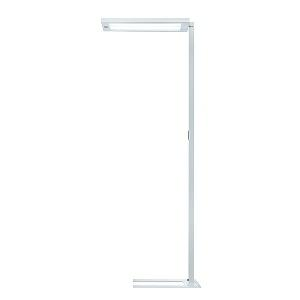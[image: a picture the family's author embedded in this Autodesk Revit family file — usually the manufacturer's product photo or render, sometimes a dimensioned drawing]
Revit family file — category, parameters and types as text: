
# Revit family: lavigo_-_dps_14000_840_r_g2_00725995_d7d4
name_source: partatom
category: Lighting Fixtures
units: mm (PartAtom-declared; Revit-internal decimal feet)

## family parameters
Cut with Voids When Loaded = No
Host = Face
Light Source = No
Part Type = Normal
Room Calculation Point = No
Round Connector Dimension = Use Diameter
Shared = No

## types (1)
- LAVIGO - DPS 14000/840/R/G2 (1 x LED, 14050 lm, 4000K)
    Apparent Load = 93 VA
    Approval mark = CE
    CIE Flux Codes = 60 87 97 12 100
    Color Rendering = 80-89
    Color Temperature = 4000K
    Control Gear = Electronic ballast
    Default Elevation = 1800 mm
    Description = DPS 14000/840/R/G2|Free-standing luminaire|light source: LED|work equipment: Electronic ballast|connected load: 220-240 V, 50/60 Hz|Power consumption: approx. 93 W|standby: approx. 0,50|power factor: approx. 0,943|luminous flux: 14050 lm|luminous efficacy: 151 lm/W|light distribution: Direct/indirect|direct ratio: approx. 12 %|colour temperature: Cold white, ca. 4000 K|color rendering index (CRI): >= 80|chromaticity tolerance:  3 SDCM|technology: Presence and daylight sensor control (PIR)|operation: Multi-function switch|luminaire body|material: Steel/plastic|surface: Painted|colour: White|lamp cover: Acrylic (PMMA), Satine|tubular section|material: Steel tube|surface: Painted|Form: Tubular section upright|colour of tubular section: White|luminaire base|Form: C-form flat|weight (net): approx. 19.7 kg|mains lead: 3.00 m Mains plug CEE 7/VII|Fastening: Floor standing base|decorative contrast side parts: Flint grey|glare control: Prism aperture|luminance(L65): <= 3000 cd/m|unified glare rating(4H 8H): <=  16|special features: Luminaire head detachable, Cradle to Cradle Certified TM, Direct light component with edge light and light-guide technology for homogenous light exit, Flicker-free, Integrated light and presence sensor PIR, Retrofittable with TALK module, Separated, direct and indirect light individually adjustable|Approval mark: VDE - ENEC|
    Frequency = 50 Hz, 60 Hz
    Height = 36 mm
    Lamp = 1 x LED
    Lamp Light Flux = 14050 lm
    Lamp count = 1
    Length = 675 mm
    Luminous efficacy = 151 lm/W
    Manufacturer = Waldmann
    ModVariant = No
    Model = 00725995
    Mounting Place = Floor
    Mounting Type = Freestanding
    Number of Poles = 1
    OnlyDefault = Yes
    Power Factor = 1
    Product Name = LAVIGO - DPS 14000/840/R/G2
    Product group = Free standing luminaire
    ProductGroupID = 13
    Protection Class = Protection class I
    Protection Degree = IP 20
    RLX_Detail_Level = 1
    RLX_Emergency_Light_Flux = 0 lm
    RLX_Emergency_Type = 0
    RLX_Emergency_Type_DB = No
    RlxData = <blob elided: 37121 chars, md5=215a879d>
    Socket = socket
    Standby Power = 0 W
    System Light Flux = 14050 lm
    System Power = 93 W
    Type Comments = Product without accessories
    Type Image = 121695000-00610208.jpg
    URL = http://relux.com
    VarID = ---
    Voltage = 230 V
    Voltage Range = 220-240 V
    Weight = 0.00 kg
    Width = 320 mm

## geometry (parser evidence)
native form markers: Blend x4, Sweep x14
no freeform markers — native parametric forms only
